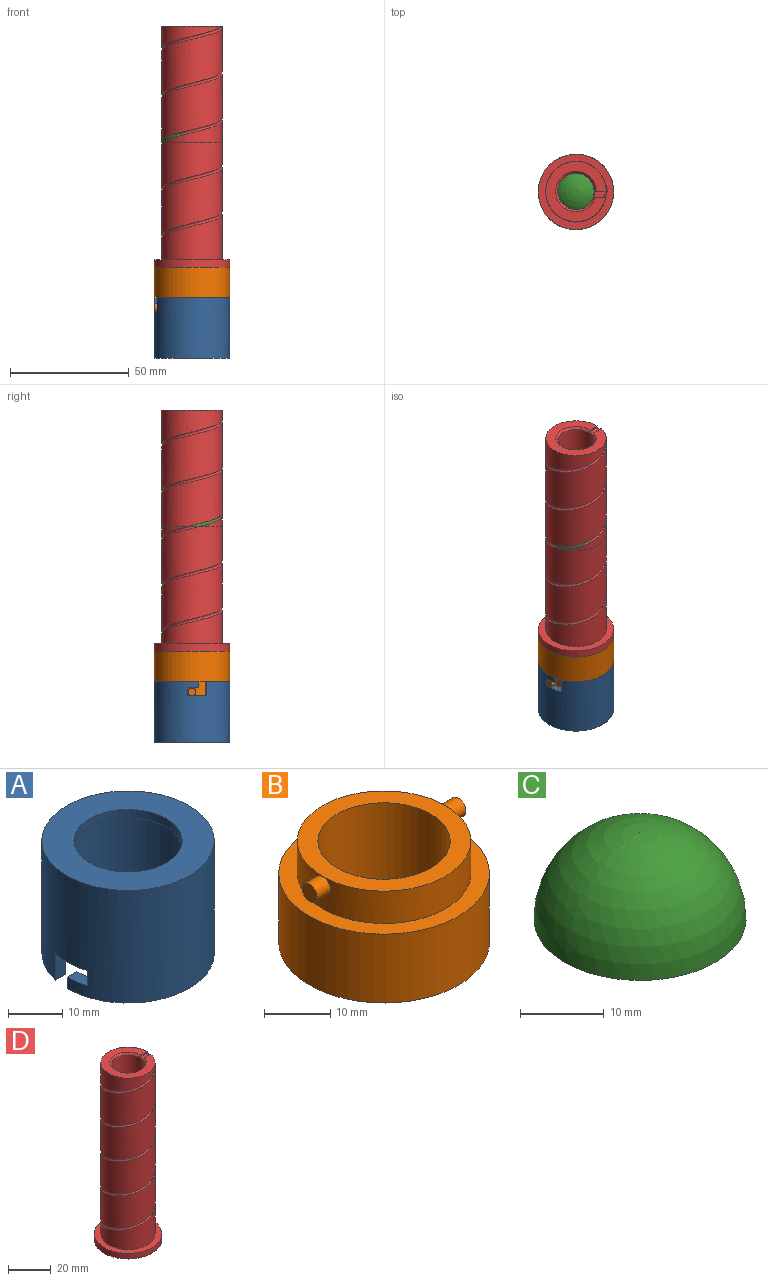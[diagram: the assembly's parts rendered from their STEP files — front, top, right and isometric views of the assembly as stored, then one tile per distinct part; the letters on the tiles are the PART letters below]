
ASSEMBLY  parts=4 mates=4
PART A: 18 faces, bbox 31.8x31.8x25.4 mm
  f0: plane 31.38x15.88mm, normal (0,0,-1), area 107.8mm2, adj f2,f7,f8,f16
  f1: plane 31.38x15.88mm, normal (0,0,-1), area 107.8mm2, adj f4,f6,f8,f17
  f2: plane 2.54x2.54mm, normal (0,-1,0), area 6.5mm2, adj f0,f8,f13,f16
  f3: plane 3.43x2.68mm, normal (0,-1,0), area 9.2mm2, adj f8,f13,f14,f16
  f4: plane 5.97x2.61mm, normal (0,1,0), area 15.6mm2, adj f1,f8,f14,f17
  f5: plane 3.43x2.68mm, normal (0,1,0), area 9.2mm2, adj f8,f14,f15,f17
  f6: plane 2.54x2.54mm, normal (0,1,0), area 6.5mm2, adj f1,f8,f15,f17
  f7: plane 5.97x2.61mm, normal (0,-1,0), area 15.6mm2, adj f0,f8,f14,f16
  f8: cylinder r=15.88mm len=31.75mm, axis (0,0,-1), area 2460.5mm2, adj f0,f1,f2,f3,f4,f5,f6,f7
  f9: cylinder r=11.56mm len=23.11mm, axis (0,0,-1), area 1272.6mm2, adj f11,f14
  f10: plane 31.75x31.75mm, normal (0,0,1), area 479.5mm2, adj f8,f12
  f11: plane 23.11x23.11mm, normal (0,0,-1), area 107.4mm2, adj f9,f12
  f12: cylinder r=9.97mm len=19.94mm, axis (0,0,1), area 119.3mm2, adj f10,f11
  f13: plane 4.57x3.35mm, normal (0,0,1), area 11.8mm2, adj f2,f3,f8,f16
  f14: plane 31.75x26.67mm, normal (0,0,-1), area 180.3mm2, adj f3,f4,f5,f7,f8,f9,f16,f17
  f15: plane 4.57x3.35mm, normal (0,0,1), area 11.8mm2, adj f5,f6,f8,f17
  f16: cylinder r=13.33mm len=26.22mm, axis (0,0,-1), area 213.4mm2, adj f0,f2,f3,f7,f13,f14
  f17: cylinder r=13.33mm len=26.22mm, axis (0,0,-1), area 213.4mm2, adj f1,f4,f5,f6,f14,f15
PART B: 10 faces, bbox 31.8x31.8x18.7 mm
  f0: cylinder r=9.97mm len=19.94mm, axis (0,0,-1), area 1169.4mm2, adj f4,f5
  f1: cylinder r=13.08mm len=26.16mm, axis (0,0,-1), area 474.7mm2, adj f3,f5,f7,f9
  f2: cylinder r=15.88mm len=31.75mm, axis (0,0,-1), area 1266.8mm2, adj f3,f4
  f3: plane 31.75x31.75mm, normal (0,0,1), area 254.2mm2, adj f1,f2
  f4: plane 31.75x31.75mm, normal (0,0,-1), area 479.5mm2, adj f0,f2
  f5: plane 26.16x26.16mm, normal (0,0,1), area 225.3mm2, adj f0,f1
  f6: plane 3.18x3.18mm, normal (1,0,0), area 7.9mm2, adj f7
  f7: cylinder r=1.59mm len=3.18mm, axis (-1,0,0), area 28.4mm2, adj f1,f6
  f8: plane 3.18x3.18mm, normal (-1,0,0), area 7.9mm2, adj f9
  f9: cylinder r=1.59mm len=3.18mm, axis (-1,0,0), area 28.4mm2, adj f1,f8
PART C: 4 faces, bbox 25.4x25.4x15.9 mm
  f0: plane 14.73x14.73mm, normal (0,0,-1), area 170.5mm2, adj f1
  f1: cylinder r=7.37mm len=14.73mm, axis (0,0,-1), area 146.9mm2, adj f0,f2
  f2: plane 25.4x25.4mm, normal (0,0,-1), area 336.3mm2, adj f1,f3
  f3: sphere r=12.7mm, area 1013.4mm2, adj f2
PART D: 13 faces, bbox 32.3x32.3x102.8 mm
  f0: plane 25.4x25.4mm, normal (0,0,1), area 268.3mm2, adj f5,f7,f10,f12
  f1: cylinder r=7.62mm len=99.44mm, axis (0,0,1), area 4761mm2, adj f11,f12
  f2: plane 31.75x31.75mm, normal (0,0,-1), area 543.4mm2, adj f3,f11
  f3: cylinder r=15.88mm len=31.75mm, axis (0,0,1), area 316.7mm2, adj f2,f4
  f4: plane 32.32x32.32mm, normal (0,0,1), area 283.7mm2, adj f3,f5,f6,f8
  f5: cylinder r=12.7mm len=98.43mm, axis (0,0,1), area 7240.7mm2, adj f0,f4,f6,f7,f8
  f6: plane 1.45x1.45mm, normal (0,1,0), area 1mm2, adj f4,f5,f8
  f7: plane 4.83x0.64mm, normal (0,-1,0), area 2.9mm2, adj f0,f5,f9,f12
  f8: bspline ~99.7x26.66mm, area 779.6mm2, adj f4,f5,f6,f9,f10
  f9: plane 5.83x3.14mm, normal (0,0,1), area 11.3mm2, adj f7,f8,f10,f12
  f10: plane 5.18x0.82mm, normal (0,1,0), area 2.6mm2, adj f0,f8,f9,f12
  f11: cone r=8.89mm half-angle=45deg, axis (0,0,-1), area 93.2mm2, adj f1,f2
  f12: cone r=7.62mm half-angle=45deg, axis (0,0,1), area 61.3mm2, adj f0,f1,f7,f9,f10
PLACE A rot(axis=(0.09,-1,0),180deg) t=(-0.05,0.08,-63.73)mm
PLACE B rot(axis=(1,0,0),180deg) t=(-0.05,0.08,-50.96)mm
PLACE C t=(-0.05,0.08,1.62)mm
PLACE D t=(-0.05,0.08,-50.96)mm fixed
MATE cylindrical A.f8 <-> B.f2  axis (0,0,1) through (-0.05,0.08,-76.43)mm
MATE planar D.f3 <-> B.f2  axis (0,0,-1) through (-0.05,0.08,-50.96)mm
MATE cylindrical B.f2 <-> D.f3  axis (0,0,1) through (-0.05,0.08,-57.31)mm
MATE cylindrical D.f1 <-> C.f1  axis (0,0,1) through (-0.05,0.08,0.03)mm
